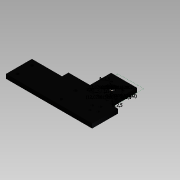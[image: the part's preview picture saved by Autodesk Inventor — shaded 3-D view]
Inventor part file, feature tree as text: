
AUTODESK INVENTOR PART (.ipt)
format: ipt  version: 2015 SP1 (Build 190203100, 203)  size: 231,936 bytes
history: native  units: mm
features: sketch x14, extrude x12, reference x5, other x2, plane x1, sweep x1, projected_geometry x1
ambient origin geometry x8: Origin, YZ Plane, XZ Plane, XY Plane, X Axis, Y Axis, Z Axis, Center Point
bodies: Solid1 (feature_tree)
feature tree (36):
  sketch  "Sketch1"  dims[d0=5.0mm d1=0.0mm d2=100.0mm]
  extrude  "Extrusion1"  Depth=100.0mm
  extrude  "Extrusion3"  Depth=30.0mm TaperAngle=0.0deg
  extrude  "Extrusion4"  Depth=10.0mm
  sketch  "Sketch6"  dims[d9=10.0mm d10=0.0mm d19=0.616194mm]
  sketch  "Sketch7"  dims[d22=30.0mm d23=5.0mm]
  plane  "Work Plane2"
  sweep  "Sweep1"
  other  "YZ 0"
  other  "XY 0"
  extrude  "Extrusion8"  Depth=6.802721mm
  extrude  "Extrusion9"  TaperAngle=90.0deg  [1 undecoded]
  extrude  "Extrusion10"  Depth=25.0mm
  extrude  "Extrusion11"  Depth=6.803mm
  extrude  "Extrusion12"  Depth=10.0mm TaperAngle=0.0deg
  extrude  "Extrusion13"  Depth=10.0mm TaperAngle=0.0deg
  extrude  "Extrusion14"  Depth=15.0mm
  extrude  "Extrusion15"  Depth=10.0mm
  extrude  "Extrusion16"  Depth=3.0mm
  sketch  "Sketch4"  dims[d6=30.0mm d7=3.5mm d8=0.0mm]
  reference  "Reference3"
  reference  "Reference4"
  reference  "Reference5"
  reference  "Reference6"
  reference  "Reference7"
  projected_geometry  "Projected Loop1"
  sketch  "Sketch9"  dims[d24=6.802721mm d25=6.802721mm]
  sketch  "Sketch12"  dims[d26=5.0mm d27=90.0deg]
  sketch  "Sketch13"  dims[d28=25.0mm d29=80.0mm]
  sketch  "Sketch15"  dims[d30=0.0mm d31=0.0mm d32=6.803mm d33=-11.25mm]
  sketch  "Sketch16"  dims[d36=10.0mm d37=0.0mm d38=10.0mm d39=0.0mm]
  sketch  "Sketch17"  dims[d40=9.0mm d41=10.0mm d42=0.0mm]
  sketch  "Sketch18"  dims[d43=15.0mm d44=15.0mm]
  sketch  "Sketch19"  dims[d45=10.0mm d46=0.0mm d47=3.0mm]
  sketch  "Sketch20"  dims[d48=3.0mm d49=3.0mm]
  sketch  "Sketch21"  dims[d50=3.0mm d51=3.315mm d52=3.315mm d53=7.071068mm d54=7.071068mm d55=7.071068mm d56=7.071068mm d57=0.0mm d64=12.020815mm d65=12.020815mm d66=12.020815mm d67=12.020815mm d68=17.0mm d69=17.0mm d70=2.5mm d71=2.5mm d72=2.5mm d73=2.5mm d74=10.0mm d75=0.0mm d76=10.0mm d77=30.0mm d78=0.0mm d79=10.0mm d80=2.5mm d81=0.0mm d82=45.0deg d83=30.0mm d84=0.0mm d85=5.0mm d86=0.0mm d87=5.0mm d88=0.0mm]
note: 1 required parameter value undecoded (feature->parameter linkage not recoverable at this tier; creation-order binding heuristic only, values carry confidence <= 0.55)
